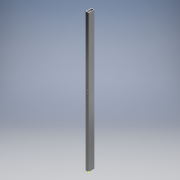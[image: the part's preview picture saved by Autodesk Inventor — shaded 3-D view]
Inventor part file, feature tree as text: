
AUTODESK INVENTOR PART (.ipt)
format: ipt  version: 2017 (Build 210142000, 142)  size: 164,352 bytes
history: native  units: in
note: dims shown in document units (in); Inventor stores cm internally (conversion verified against a paired STEP export)
features: sketch x8, extrude x3, hole x3
ambient origin geometry x8: Origin, YZ Plane, XZ Plane, XY Plane, X Axis, Y Axis, Z Axis, Center Point
bodies: Solid1 (feature_tree)
feature tree (14):
  extrude  "Extrusion1"  Depth=2.0in
  extrude  "Extrusion2"  Depth=1.75in
  extrude  "Extrusion3"  Depth=0.125in
  hole  "Hole1"  [1 undecoded]
  hole  "Hole3"  [1 undecoded]
  sketch  "Sketch8"  dims[d13=0.25in d14=48.0in d15=0.0in]
  sketch  "Sketch9"  dims[d16=1.125in]
  hole  "Hole4"  [1 undecoded]
  sketch  "Sketch2"  dims[d2=1.0in d3=2.0in]
  sketch  "Sketch3"  dims[d4=0.75in d5=1.75in]
  sketch  "Sketch4"  dims[d6=0.125in d7=0.125in]
  sketch  "Sketch5"  dims[d8=48.0in d9=0.0in d10=48.0in]
  sketch  "Sketch7"  dims[d11=24.0in d12=0.5in]
  sketch  "Sketch10"  dims[d17=1.125in d18=0.25in d19=0.0in d20=4.5in d21=0.5in d22=0.125in d24=0.125in d25=0.75in d26=0.375in d27=0.25in d28=0.5635in d29=0.125in d30=0.8108in d41=1.125in d42=0.75in d43=0.375in d44=0.25in d45=0.5635in d46=0.125in d47=0.8108in d48=23.5in d49=0.25in d50=1.0in d51=23.5in d52=24.0in d53=0.25in d54=0.75in d55=0.375in d56=0.25in d57=0.5635in d58=1.0in d59=0.8108in]
note: 3 required parameter values undecoded (feature->parameter linkage not recoverable at this tier; creation-order binding heuristic only, values carry confidence <= 0.55)
